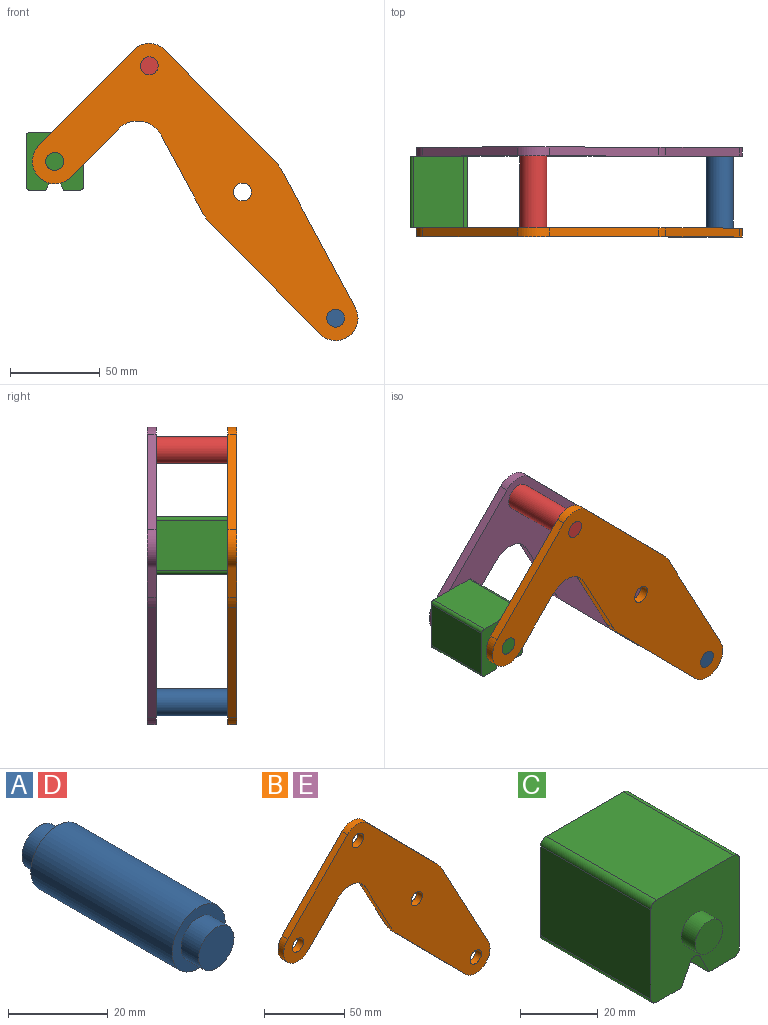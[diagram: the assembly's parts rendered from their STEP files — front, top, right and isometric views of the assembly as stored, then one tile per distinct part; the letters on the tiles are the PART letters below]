
ASSEMBLY  parts=5 mates=3
PART A: 7 faces, bbox 15x50x15 mm
  f0: cylinder r=7.5mm len=40mm, axis (0,-1,0), area 1885mm2, adj f2,f5
  f1: cylinder r=5mm len=10mm, axis (0,1,0), area 157.1mm2, adj f2,f3
  f2: plane 15x15mm, normal (0,-1,0), area 98.2mm2, adj f0,f1
  f3: plane 10x10mm, normal (0,-1,0), area 78.5mm2, adj f1
  f4: cylinder r=5mm len=10mm, axis (0,-1,0), area 157.1mm2, adj f5,f6
  f5: plane 15x15mm, normal (0,1,0), area 98.2mm2, adj f0,f4
  f6: plane 10x10mm, normal (0,1,0), area 78.5mm2, adj f4
PART B: 18 faces, bbox 181.7x5x165.8 mm
  f0: plane 43.49x23.35mm, normal (-0.88,0,-0.47), area 246.8mm2, adj f1,f14,f16,f17
  f1: cylinder r=25mm len=5.75mm, axis (0,1,0), area 35.8mm2, adj f0,f2,f16,f17
  f2: plane 61.6x60.87mm, normal (-0.71,0,-0.7), area 433mm2, adj f1,f3,f16,f17
  f3: cylinder r=12.5mm len=21.39mm, axis (0,1,0), area 178.4mm2, adj f2,f4,f16,f17
  f4: plane 76.3x40.96mm, normal (0.88,0,0.47), area 433mm2, adj f3,f5,f16,f17
  f5: cylinder r=25mm len=5.75mm, axis (0,1,0), area 35.8mm2, adj f4,f6,f16,f17
  f6: plane 61.6x60.87mm, normal (0.71,0,0.7), area 433mm2, adj f5,f7,f16,f17
  f7: cylinder r=12.5mm len=17.78mm, axis (0,1,0), area 98.9mm2, adj f6,f8,f16,f17
  f8: plane 53.35x52.71mm, normal (-0.71,0,0.7), area 375mm2, adj f7,f9,f16,f17
  f9: cylinder r=12.5mm len=21.39mm, axis (0,1,0), area 196.3mm2, adj f8,f10,f16,f17
  f10: plane 26.86x26.54mm, normal (0.71,0,-0.7), area 188.8mm2, adj f9,f14,f16,f17
  f11: cylinder r=5mm len=10mm, axis (0,1,0), area 157.1mm2, adj f16,f17
  f12: cylinder r=5mm len=10mm, axis (0,1,0), area 157.1mm2, adj f16,f17
  f13: cylinder r=5mm len=10mm, axis (0,1,0), area 157.1mm2, adj f16,f17
  f14: cylinder r=15mm len=23.89mm, axis (0,1,0), area 140.2mm2, adj f0,f10,f16,f17
  f15: cylinder r=5mm len=10mm, axis (0,1,0), area 157.1mm2, adj f16,f17
  f16: plane 181.66x165.78mm, normal (0,-1,0), area 8710.1mm2, adj f0,f1,f2,f3,f4,f5,f6,f7
  f17: plane 181.66x165.78mm, normal (0,1,0), area 8710.1mm2, adj f0,f1,f2,f3,f4,f5,f6,f7
PART C: 18 faces, bbox 32.1x50x32.1 mm
  f0: plane 40x28.08mm, normal (1,0,0), area 1123.1mm2, adj f4,f10,f13,f14
  f1: plane 40x9.04mm, normal (0,0,-1), area 361.6mm2, adj f2,f4,f10,f14
  f2: plane 40x6.42mm, normal (-0.89,0,-0.45), area 287.2mm2, adj f1,f4,f10,f15
  f3: plane 40x6.42mm, normal (0.89,0,-0.45), area 287.2mm2, adj f4,f5,f10,f15
  f4: plane 32.08x32.08mm, normal (0,-1,0), area 900.6mm2, adj f0,f1,f2,f3,f5,f6,f7,f9
  f5: plane 40x9.04mm, normal (0,0,-1), area 361.6mm2, adj f3,f4,f10,f16
  f6: plane 40x28.08mm, normal (0,0,1), area 1123.1mm2, adj f4,f10,f13,f17
  f7: plane 40x28.08mm, normal (-1,0,0), area 1123.1mm2, adj f4,f10,f16,f17
  f8: plane 10x10mm, normal (0,-1,0), area 78.5mm2, adj f9
  f9: cylinder r=5mm len=10mm, axis (0,1,0), area 157.1mm2, adj f4,f8
  f10: plane 32.08x32.08mm, normal (0,1,0), area 900.6mm2, adj f0,f1,f2,f3,f5,f6,f7,f12
  f11: plane 10x10mm, normal (0,1,0), area 78.5mm2, adj f12
  f12: cylinder r=5mm len=10mm, axis (0,-1,0), area 157.1mm2, adj f10,f11
  f13: cylinder r=2mm len=40mm, axis (0,1,0), area 125.7mm2, adj f0,f4,f6,f10
  f14: cylinder r=2mm len=40mm, axis (0,-1,0), area 125.7mm2, adj f0,f1,f4,f10
  f15: cylinder r=2mm len=40mm, axis (0,1,0), area 177.1mm2, adj f2,f3,f4,f10
  f16: cylinder r=2mm len=40mm, axis (0,1,0), area 125.7mm2, adj f4,f5,f7,f10
  f17: cylinder r=2mm len=40mm, axis (0,-1,0), area 125.7mm2, adj f4,f6,f7,f10
PART D: same geometry as A
PART E: same geometry as B
PLACE A t=(96.98,-61.52,-129.9)mm
PLACE B t=(-6.98,-61.52,10.88)mm fixed
PLACE C t=(-6.98,-61.52,10.88)mm
PLACE D t=(-6.98,-61.52,10.88)mm
PLACE E t=(-6.98,-16.52,10.88)mm
MATE revolute C.f9 <-> B.f9  axis (0,-1,0) through (-111.66,-61.52,27.92)mm
MATE fastened B.f3 <-> A.f0  axis (0,-1,0) through (45,-66.52,-59.51)mm
MATE fastened E.f7 <-> D.f0  axis (0,1,0) through (-58.95,-16.52,81.27)mm
